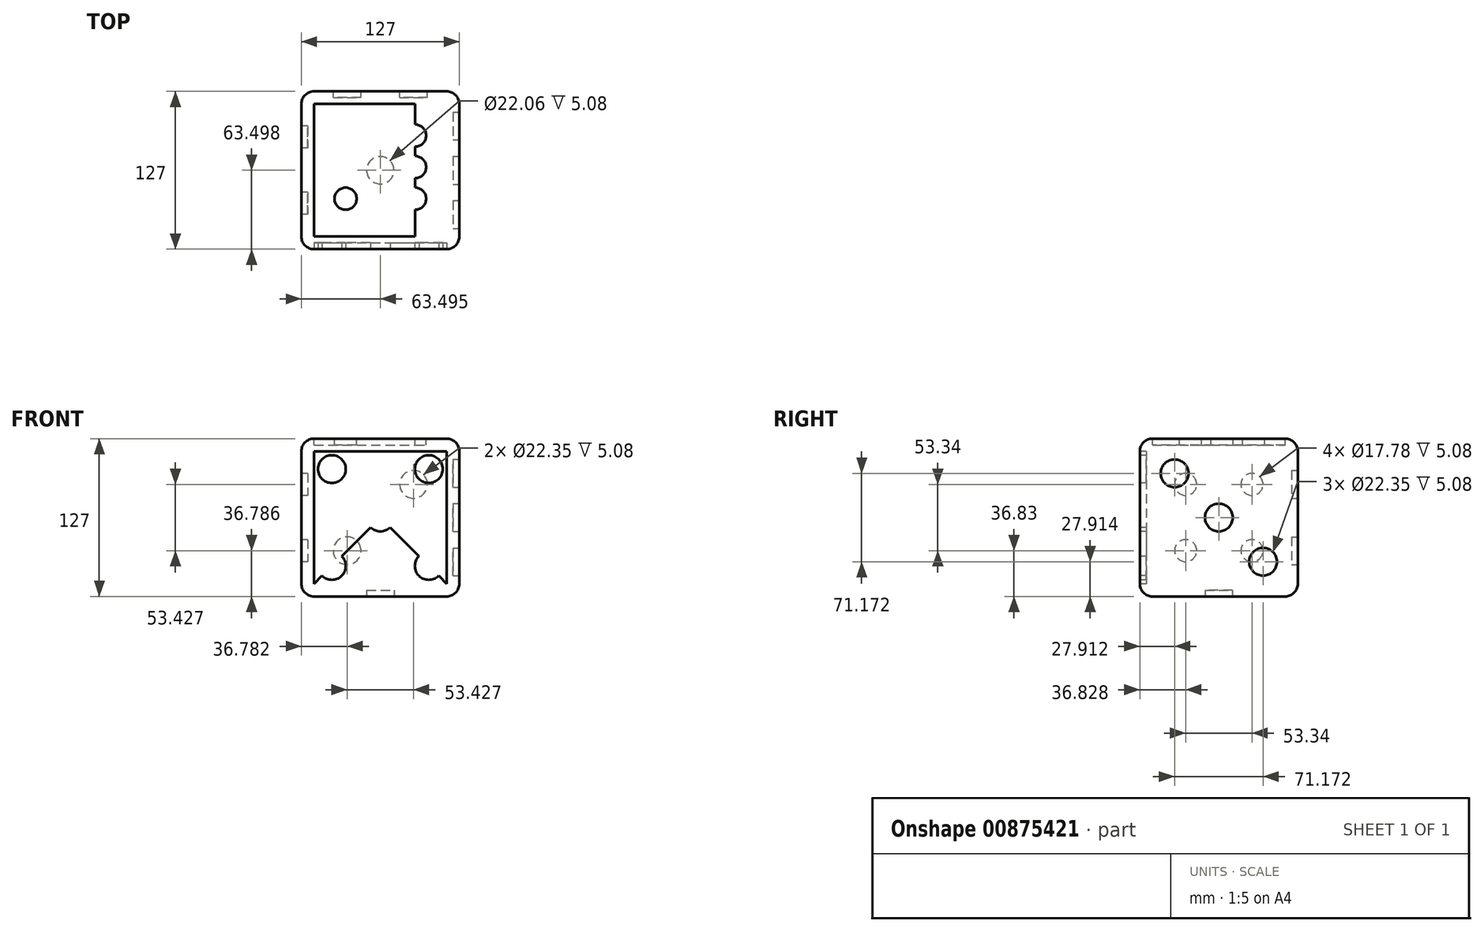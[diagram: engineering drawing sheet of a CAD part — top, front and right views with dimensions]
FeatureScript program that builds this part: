
annotation { "Feature Type Name" : "Feature", "Feature Type Description" : "" }
export const myFeature = defineFeature(function(context is Context, id is Id, definition is map)
    precondition{}
    {
        {
            var Q0;
            Q0=qCreatedBy(makeId("Top.planeOp"),FACE);
            var sketch = newSketch(context, id + "F0", { "sketchPlane" : qUnion([Q0])});
            skLineSegment(sketch, "E0.bottom", {"start": v(-135.56, 105.72) * mm, "end": v(-8.56, 105.72) * mm});
            skLineSegment(sketch, "E0.top", {"start": v(-135.56, -21.28) * mm, "end": v(-8.56, -21.28) * mm});
            skLineSegment(sketch, "E0.left", {"start": v(-135.56, 105.72) * mm, "end": v(-135.56, -21.28) * mm});
            skLineSegment(sketch, "E0.right", {"start": v(-8.56, 105.72) * mm, "end": v(-8.56, -21.28) * mm});
            skSolve(sketch);
        }
        {
            var Q0;
            Q0=makeQuery(id+"F0.imprint","IMPRINT",FACE,{"disambiguationData":[TD([[makeQuery(id+"F0.imprint","IMPRINT",EDGE,{"derivedFrom":sQuery(id+"F0.wireOp",EDGE,"E0.bottom")}),-1.0]])]});
            extrude(context, id + "F1", {"entities" : qUnion([Q0]), "depth" : 127 * mm, "offsetDistance" : 25.4 * mm});
        }
        {
            var Q0;
            Q0=makeQuery(id+"F1.opExtrude","SWEPT_FACE",FACE,{"disambiguationData":[OSD([sQuery(id+"F0.wireOp",EDGE,"E0.top")])]});
            var Q1;
            Q1=makeQuery(id+"F1.opExtrude","CAP_EDGE",EDGE,{"disambiguationData":[OSD([sQuery(id+"F0.wireOp",EDGE,"E0.bottom")])],"isStart":false});
            var Q2;
            Q2=makeQuery(id+"F1.opExtrude","CAP_FACE",FACE,{"disambiguationData":[OSD([sQuery(id+"F0.wireOp",EDGE,"E0.bottom"),sQuery(id+"F0.wireOp",EDGE,"E0.top"),sQuery(id+"F0.wireOp",EDGE,"E0.left"),sQuery(id+"F0.wireOp",EDGE,"E0.right")])],"isStart":false});
            var Q3;
            Q3=makeQuery(id+"F1.opExtrude","SWEPT_FACE",FACE,{"disambiguationData":[OSD([sQuery(id+"F0.wireOp",EDGE,"E0.left")])]});
            var Q4;
            Q4=makeQuery(id+"F1.opExtrude","SWEPT_FACE",FACE,{"disambiguationData":[OSD([sQuery(id+"F0.wireOp",EDGE,"E0.bottom")])]});
            var Q5;
            Q5=makeQuery(id+"F1.opExtrude","SWEPT_FACE",FACE,{"disambiguationData":[OSD([sQuery(id+"F0.wireOp",EDGE,"E0.right")])]});
            fillet(context, id + "F2", {"entities" : qUnion([Q0, Q1, Q2, Q3, Q4, Q5]), "radius" : 10.16 * mm, "tangentPropagation" : true, "allowEdgeOverflow" : false});
        }
        {
            var Q0;
            Q0=makeQuery(id+"F1.opExtrude","CAP_FACE",FACE,{"disambiguationData":[OSD([sQuery(id+"F0.wireOp",EDGE,"E0.bottom"),sQuery(id+"F0.wireOp",EDGE,"E0.top"),sQuery(id+"F0.wireOp",EDGE,"E0.left"),sQuery(id+"F0.wireOp",EDGE,"E0.right")])],"isStart":true});
            var sketch = newSketch(context, id + "F3", { "sketchPlane" : qUnion([Q0])});
            skPoint(sketch, "E1.0", {"position": v(-72.06, 11.12) * mm});
            skLineSegment(sketch, "E2.0", {"start": v(-125.4, 11.12) * mm, "end": v(-125.4, -95.56) * mm});
            skLineSegment(sketch, "E3.0", {"start": v(-18.72, -95.56) * mm, "end": v(-18.72, 11.12) * mm});
            skLineSegment(sketch, "E4.0", {"start": v(-125.4, -95.56) * mm, "end": v(-18.72, -95.56) * mm});
            skLineSegment(sketch, "E5", {"start": v(-72.06, 11.12) * mm, "end": v(-72.06, -95.56) * mm, "construction": true});
            skLineSegment(sketch, "E6", {"start": v(-125.4, -42.22) * mm, "end": v(-18.72, -42.22) * mm, "construction": true});
            skCircle(sketch, "E7", {"center": v(-72.06, -42.22) * mm, "radius": 11.03 * mm});
            skSolve(sketch);
        }
        {
            var Q0;
            Q0=makeQuery(id+"F3.imprint","IMPRINT",FACE,{"disambiguationData":[TD([[makeQuery(id+"F3.imprint","IMPRINT",EDGE,{"derivedFrom":sQuery(id+"F3.wireOp",EDGE,"E7")}),1.0]])]});
            extrude(context, id + "F4", {"entities" : qUnion([Q0]), "operationType" : NewBodyOperationType.REMOVE, "oppositeDirection" : true, "depth" : 5.08 * mm, "offsetDistance" : 25.4 * mm});
        }
        {
            var Q0;
            Q0=makeQuery(id+"F1.opExtrude","CAP_FACE",FACE,{"disambiguationData":[OSD([sQuery(id+"F0.wireOp",EDGE,"E0.bottom"),sQuery(id+"F0.wireOp",EDGE,"E0.top"),sQuery(id+"F0.wireOp",EDGE,"E0.left"),sQuery(id+"F0.wireOp",EDGE,"E0.right")])],"isStart":false});
            var sketch = newSketch(context, id + "F5", { "sketchPlane" : qUnion([Q0])});
            skLineSegment(sketch, "E8.0", {"start": v(-125.4, -11.12) * mm, "end": v(-18.72, -11.12) * mm});
            skLineSegment(sketch, "E9.0", {"start": v(-18.72, -11.12) * mm, "end": v(-18.72, 95.56) * mm});
            skLineSegment(sketch, "E10.0", {"start": v(-18.72, 95.56) * mm, "end": v(-125.4, 95.56) * mm});
            skLineSegment(sketch, "E11.0", {"start": v(-125.4, 95.56) * mm, "end": v(-125.4, -11.12) * mm});
            skLineSegment(sketch, "E12", {"start": v(-100, 95.56) * mm, "end": v(-100, -11.12) * mm});
            skLineSegment(sketch, "E13", {"start": v(-44.12, -11.12) * mm, "end": v(-44.12, 95.56) * mm});
            skCircle(sketch, "E14", {"center": v(-100, 70.16) * mm, "radius": 8.9 * mm});
            skCircle(sketch, "E15", {"center": v(-100, 19.36) * mm, "radius": 8.9 * mm});
            skCircle(sketch, "E16", {"center": v(-100, 44.76) * mm, "radius": 8.9 * mm});
            skCircle(sketch, "E17", {"center": v(-44.12, 70.16) * mm, "radius": 8.9 * mm});
            skCircle(sketch, "E18", {"center": v(-44.12, 44.76) * mm, "radius": 8.9 * mm});
            skCircle(sketch, "E19", {"center": v(-44.12, 19.36) * mm, "radius": 8.9 * mm});
            skSolve(sketch);
        }
        {
            var Q0;
            {var subQ0=sQuery(id+"F5.wireOp",EDGE,"E14");var subQ1=sQuery(id+"F5.wireOp",EDGE,"E12");var subQ2=makeQuery(id+"F5.imprint","INTERSECT",VERTEX,{"disambiguationData":[OD(0.0)],"derivedFrom":[subQ1,subQ0]});Q0=makeQuery(id+"F5.imprint","IMPRINT",FACE,{"disambiguationData":[TD([[makeQuery(id+"F5.imprint","IMPRINT",EDGE,{"disambiguationData":[TD([[subQ2,-1.0]])],"derivedFrom":subQ1}),-1.0]])]});}
            var Q1;
            {var subQ0=sQuery(id+"F5.wireOp",EDGE,"E14");var subQ1=sQuery(id+"F5.wireOp",EDGE,"E12");var subQ2=makeQuery(id+"F5.imprint","INTERSECT",VERTEX,{"disambiguationData":[OD(0.0)],"derivedFrom":[subQ1,subQ0]});Q1=makeQuery(id+"F5.imprint","IMPRINT",FACE,{"disambiguationData":[TD([[makeQuery(id+"F5.imprint","IMPRINT",EDGE,{"disambiguationData":[TD([[subQ2,-1.0]])],"derivedFrom":subQ1}),1.0]])]});}
            var Q2;
            {var subQ0=sQuery(id+"F5.wireOp",EDGE,"E16");var subQ1=sQuery(id+"F5.wireOp",EDGE,"E12");var subQ2=makeQuery(id+"F5.imprint","INTERSECT",VERTEX,{"disambiguationData":[OD(0.0)],"derivedFrom":[subQ1,subQ0]});Q2=makeQuery(id+"F5.imprint","IMPRINT",FACE,{"disambiguationData":[TD([[makeQuery(id+"F5.imprint","IMPRINT",EDGE,{"disambiguationData":[TD([[subQ2,-1.0]])],"derivedFrom":subQ1}),-1.0]])]});}
            var Q3;
            {var subQ0=sQuery(id+"F5.wireOp",EDGE,"E16");var subQ1=sQuery(id+"F5.wireOp",EDGE,"E12");var subQ2=makeQuery(id+"F5.imprint","INTERSECT",VERTEX,{"disambiguationData":[OD(0.0)],"derivedFrom":[subQ1,subQ0]});Q3=makeQuery(id+"F5.imprint","IMPRINT",FACE,{"disambiguationData":[TD([[makeQuery(id+"F5.imprint","IMPRINT",EDGE,{"disambiguationData":[TD([[subQ2,-1.0]])],"derivedFrom":subQ1}),1.0]])]});}
            var Q4;
            {var subQ0=sQuery(id+"F5.wireOp",EDGE,"E17");var subQ1=sQuery(id+"F5.wireOp",EDGE,"E13");var subQ2=makeQuery(id+"F5.imprint","INTERSECT",VERTEX,{"disambiguationData":[OD(0.0)],"derivedFrom":[subQ1,subQ0]});Q4=makeQuery(id+"F5.imprint","IMPRINT",FACE,{"disambiguationData":[TD([[makeQuery(id+"F5.imprint","IMPRINT",EDGE,{"disambiguationData":[TD([[subQ2,-1.0]])],"derivedFrom":subQ1}),1.0]])]});}
            var Q5;
            {var subQ0=sQuery(id+"F5.wireOp",EDGE,"E17");var subQ1=sQuery(id+"F5.wireOp",EDGE,"E13");var subQ2=makeQuery(id+"F5.imprint","INTERSECT",VERTEX,{"disambiguationData":[OD(0.0)],"derivedFrom":[subQ1,subQ0]});Q5=makeQuery(id+"F5.imprint","IMPRINT",FACE,{"disambiguationData":[TD([[makeQuery(id+"F5.imprint","IMPRINT",EDGE,{"disambiguationData":[TD([[subQ2,-1.0]])],"derivedFrom":subQ1}),-1.0]])]});}
            var Q6;
            {var subQ0=sQuery(id+"F5.wireOp",EDGE,"E18");var subQ1=sQuery(id+"F5.wireOp",EDGE,"E13");var subQ2=makeQuery(id+"F5.imprint","INTERSECT",VERTEX,{"disambiguationData":[OD(0.0)],"derivedFrom":[subQ1,subQ0]});Q6=makeQuery(id+"F5.imprint","IMPRINT",FACE,{"disambiguationData":[TD([[makeQuery(id+"F5.imprint","IMPRINT",EDGE,{"disambiguationData":[TD([[subQ2,-1.0]])],"derivedFrom":subQ1}),1.0]])]});}
            var Q7;
            {var subQ0=sQuery(id+"F5.wireOp",EDGE,"E18");var subQ1=sQuery(id+"F5.wireOp",EDGE,"E13");var subQ2=makeQuery(id+"F5.imprint","INTERSECT",VERTEX,{"disambiguationData":[OD(0.0)],"derivedFrom":[subQ1,subQ0]});Q7=makeQuery(id+"F5.imprint","IMPRINT",FACE,{"disambiguationData":[TD([[makeQuery(id+"F5.imprint","IMPRINT",EDGE,{"disambiguationData":[TD([[subQ2,-1.0]])],"derivedFrom":subQ1}),-1.0]])]});}
            var Q8;
            {var subQ0=sQuery(id+"F5.wireOp",EDGE,"E15");var subQ1=sQuery(id+"F5.wireOp",EDGE,"E12");var subQ2=makeQuery(id+"F5.imprint","INTERSECT",VERTEX,{"disambiguationData":[OD(0.0)],"derivedFrom":[subQ1,subQ0]});Q8=makeQuery(id+"F5.imprint","IMPRINT",FACE,{"disambiguationData":[TD([[makeQuery(id+"F5.imprint","IMPRINT",EDGE,{"disambiguationData":[TD([[subQ2,-1.0]])],"derivedFrom":subQ1}),-1.0]])]});}
            var Q9;
            {var subQ0=sQuery(id+"F5.wireOp",EDGE,"E15");var subQ1=sQuery(id+"F5.wireOp",EDGE,"E12");var subQ2=makeQuery(id+"F5.imprint","INTERSECT",VERTEX,{"disambiguationData":[OD(0.0)],"derivedFrom":[subQ1,subQ0]});Q9=makeQuery(id+"F5.imprint","IMPRINT",FACE,{"disambiguationData":[TD([[makeQuery(id+"F5.imprint","IMPRINT",EDGE,{"disambiguationData":[TD([[subQ2,-1.0]])],"derivedFrom":subQ1}),1.0]])]});}
            var Q10;
            {var subQ0=sQuery(id+"F5.wireOp",EDGE,"E19");var subQ1=sQuery(id+"F5.wireOp",EDGE,"E13");var subQ2=makeQuery(id+"F5.imprint","INTERSECT",VERTEX,{"disambiguationData":[OD(0.0)],"derivedFrom":[subQ1,subQ0]});Q10=makeQuery(id+"F5.imprint","IMPRINT",FACE,{"disambiguationData":[TD([[makeQuery(id+"F5.imprint","IMPRINT",EDGE,{"disambiguationData":[TD([[subQ2,-1.0]])],"derivedFrom":subQ1}),1.0]])]});}
            var Q11;
            {var subQ0=sQuery(id+"F5.wireOp",EDGE,"E19");var subQ1=sQuery(id+"F5.wireOp",EDGE,"E13");var subQ2=makeQuery(id+"F5.imprint","INTERSECT",VERTEX,{"disambiguationData":[OD(0.0)],"derivedFrom":[subQ1,subQ0]});Q11=makeQuery(id+"F5.imprint","IMPRINT",FACE,{"disambiguationData":[TD([[makeQuery(id+"F5.imprint","IMPRINT",EDGE,{"disambiguationData":[TD([[subQ2,-1.0]])],"derivedFrom":subQ1}),-1.0]])]});}
            extrude(context, id + "F6", {"entities" : qUnion([Q0, Q1, Q2, Q3, Q4, Q5, Q6, Q7, Q8, Q9, Q10, Q11]), "operationType" : NewBodyOperationType.REMOVE, "oppositeDirection" : true, "depth" : 5.08 * mm, "offsetDistance" : 25.4 * mm});
        }
        {
            var Q0;
            Q0=makeQuery(id+"F1.opExtrude","SWEPT_FACE",FACE,{"disambiguationData":[OSD([sQuery(id+"F0.wireOp",EDGE,"E0.left")])]});
            var sketch = newSketch(context, id + "F7", { "sketchPlane" : qUnion([Q0])});
            skLineSegment(sketch, "E20.0", {"start": v(11.12, 116.84) * mm, "end": v(-95.56, 116.84) * mm});
            skLineSegment(sketch, "E21.0", {"start": v(-95.56, 116.84) * mm, "end": v(-95.56, 10.16) * mm});
            skLineSegment(sketch, "E22.0", {"start": v(11.12, 10.16) * mm, "end": v(11.12, 116.84) * mm});
            skLineSegment(sketch, "E23.0", {"start": v(-95.56, 10.16) * mm, "end": v(11.12, 10.16) * mm});
            skCircle(sketch, "E24", {"center": v(-68.89, 90.17) * mm, "radius": 8.9 * mm});
            skCircle(sketch, "E25", {"center": v(-15.55, 90.17) * mm, "radius": 8.9 * mm});
            skCircle(sketch, "E26", {"center": v(-68.89, 36.83) * mm, "radius": 8.9 * mm});
            skCircle(sketch, "E27", {"center": v(-15.55, 36.83) * mm, "radius": 8.9 * mm});
            skSolve(sketch);
        }
        {
            var Q0;
            Q0=makeQuery(id+"F7.imprint","IMPRINT",FACE,{"disambiguationData":[TD([[makeQuery(id+"F7.imprint","IMPRINT",EDGE,{"derivedFrom":sQuery(id+"F7.wireOp",EDGE,"E24")}),1.0]])]});
            var Q1;
            Q1=makeQuery(id+"F7.imprint","IMPRINT",FACE,{"disambiguationData":[TD([[makeQuery(id+"F7.imprint","IMPRINT",EDGE,{"derivedFrom":sQuery(id+"F7.wireOp",EDGE,"E26")}),1.0]])]});
            var Q2;
            Q2=makeQuery(id+"F7.imprint","IMPRINT",FACE,{"disambiguationData":[TD([[makeQuery(id+"F7.imprint","IMPRINT",EDGE,{"derivedFrom":sQuery(id+"F7.wireOp",EDGE,"E27")}),1.0]])]});
            var Q3;
            Q3=makeQuery(id+"F7.imprint","IMPRINT",FACE,{"disambiguationData":[TD([[makeQuery(id+"F7.imprint","IMPRINT",EDGE,{"derivedFrom":sQuery(id+"F7.wireOp",EDGE,"E25")}),1.0]])]});
            extrude(context, id + "F8", {"entities" : qUnion([Q0, Q1, Q2, Q3]), "operationType" : NewBodyOperationType.REMOVE, "oppositeDirection" : true, "depth" : 5.08 * mm, "offsetDistance" : 25.4 * mm});
        }
        {
            var Q0;
            Q0=makeQuery(id+"F1.opExtrude","SWEPT_FACE",FACE,{"disambiguationData":[OSD([sQuery(id+"F0.wireOp",EDGE,"E0.right")])]});
            var sketch = newSketch(context, id + "F9", { "sketchPlane" : qUnion([Q0])});
            skCircle(sketch, "E28", {"center": v(77.8, 27.91) * mm, "radius": 11.18 * mm});
            skCircle(sketch, "E29", {"center": v(6.63, 99.09) * mm, "radius": 11.18 * mm});
            skCircle(sketch, "E30", {"center": v(42.22, 63.5) * mm, "radius": 11.18 * mm});
            skSolve(sketch);
        }
        {
            var Q0;
            Q0=makeQuery(id+"F9.imprint","IMPRINT",FACE,{"disambiguationData":[TD([[makeQuery(id+"F9.imprint","IMPRINT",EDGE,{"derivedFrom":sQuery(id+"F9.wireOp",EDGE,"E29")}),1.0]])]});
            var Q1;
            Q1=makeQuery(id+"F9.imprint","IMPRINT",FACE,{"disambiguationData":[TD([[makeQuery(id+"F9.imprint","IMPRINT",EDGE,{"derivedFrom":sQuery(id+"F9.wireOp",EDGE,"E28")}),1.0]])]});
            var Q2;
            Q2=makeQuery(id+"F9.imprint","IMPRINT",FACE,{"disambiguationData":[TD([[makeQuery(id+"F9.imprint","IMPRINT",EDGE,{"derivedFrom":sQuery(id+"F9.wireOp",EDGE,"E30")}),1.0]])]});
            extrude(context, id + "F10", {"entities" : qUnion([Q0, Q1, Q2]), "operationType" : NewBodyOperationType.REMOVE, "oppositeDirection" : true, "depth" : 5.08 * mm, "offsetDistance" : 25.4 * mm});
        }
        {
            var Q0;
            Q0=makeQuery(id+"F1.opExtrude","SWEPT_FACE",FACE,{"disambiguationData":[OSD([sQuery(id+"F0.wireOp",EDGE,"E0.top")])]});
            var sketch = newSketch(context, id + "F11", { "sketchPlane" : qUnion([Q0])});
            skLineSegment(sketch, "E31", {"start": v(-125.4, 116.84) * mm, "end": v(-18.72, 10.16) * mm});
            skLineSegment(sketch, "E32", {"start": v(-18.72, 116.84) * mm, "end": v(-125.4, 10.16) * mm});
            skCircle(sketch, "E33", {"center": v(-72.06, 63.5) * mm, "radius": 11.18 * mm});
            skCircle(sketch, "E34", {"center": v(-111.04, 102.47) * mm, "radius": 11.18 * mm});
            skCircle(sketch, "E35", {"center": v(-111.04, 24.53) * mm, "radius": 11.18 * mm});
            skCircle(sketch, "E36", {"center": v(-33.1, 24.53) * mm, "radius": 11.18 * mm});
            skCircle(sketch, "E37", {"center": v(-33.1, 102.47) * mm, "radius": 11.18 * mm});
            skSolve(sketch);
        }
        {
            var Q0;
            {var subQ0=sQuery(id+"F11.wireOp",EDGE,"E34");var subQ1=sQuery(id+"F11.wireOp",EDGE,"E31");var subQ2=makeQuery(id+"F11.imprint","INTERSECT",VERTEX,{"disambiguationData":[OD(0.0)],"derivedFrom":[subQ1,subQ0]});Q0=makeQuery(id+"F11.imprint","IMPRINT",FACE,{"disambiguationData":[TD([[makeQuery(id+"F11.imprint","IMPRINT",EDGE,{"disambiguationData":[TD([[subQ2,-1.0]])],"derivedFrom":subQ1}),1.0]])]});}
            var Q1;
            {var subQ0=sQuery(id+"F11.wireOp",EDGE,"E36");var subQ1=sQuery(id+"F11.wireOp",EDGE,"E31");var subQ2=makeQuery(id+"F11.imprint","INTERSECT",VERTEX,{"disambiguationData":[OD(0.0)],"derivedFrom":[subQ1,subQ0]});Q1=makeQuery(id+"F11.imprint","IMPRINT",FACE,{"disambiguationData":[TD([[makeQuery(id+"F11.imprint","IMPRINT",EDGE,{"disambiguationData":[TD([[subQ2,-1.0]])],"derivedFrom":subQ1}),-1.0]])]});}
            var Q2;
            {var subQ0=sQuery(id+"F11.wireOp",EDGE,"E36");var subQ1=sQuery(id+"F11.wireOp",EDGE,"E31");var subQ2=makeQuery(id+"F11.imprint","INTERSECT",VERTEX,{"disambiguationData":[OD(0.0)],"derivedFrom":[subQ1,subQ0]});Q2=makeQuery(id+"F11.imprint","IMPRINT",FACE,{"disambiguationData":[TD([[makeQuery(id+"F11.imprint","IMPRINT",EDGE,{"disambiguationData":[TD([[subQ2,-1.0]])],"derivedFrom":subQ1}),1.0]])]});}
            var Q3;
            {var subQ0=sQuery(id+"F11.wireOp",EDGE,"E35");var subQ1=sQuery(id+"F11.wireOp",EDGE,"E32");var subQ2=makeQuery(id+"F11.imprint","INTERSECT",VERTEX,{"disambiguationData":[OD(0.0)],"derivedFrom":[subQ1,subQ0]});Q3=makeQuery(id+"F11.imprint","IMPRINT",FACE,{"disambiguationData":[TD([[makeQuery(id+"F11.imprint","IMPRINT",EDGE,{"disambiguationData":[TD([[subQ2,-1.0]])],"derivedFrom":subQ1}),-1.0]])]});}
            var Q4;
            {var subQ0=sQuery(id+"F11.wireOp",EDGE,"E35");var subQ1=sQuery(id+"F11.wireOp",EDGE,"E32");var subQ2=makeQuery(id+"F11.imprint","INTERSECT",VERTEX,{"disambiguationData":[OD(0.0)],"derivedFrom":[subQ1,subQ0]});Q4=makeQuery(id+"F11.imprint","IMPRINT",FACE,{"disambiguationData":[TD([[makeQuery(id+"F11.imprint","IMPRINT",EDGE,{"disambiguationData":[TD([[subQ2,-1.0]])],"derivedFrom":subQ1}),1.0]])]});}
            var Q5;
            {var subQ0=sQuery(id+"F11.wireOp",EDGE,"E33");var subQ1=sQuery(id+"F11.wireOp",EDGE,"E31");var subQ2=makeQuery(id+"F11.imprint","INTERSECT",VERTEX,{"disambiguationData":[OD(0.0)],"derivedFrom":[subQ1,subQ0]});Q5=makeQuery(id+"F11.imprint","IMPRINT",FACE,{"disambiguationData":[TD([[makeQuery(id+"F11.imprint","IMPRINT",EDGE,{"disambiguationData":[TD([[subQ2,-1.0]])],"derivedFrom":subQ1}),1.0]])]});}
            var Q6;
            {var subQ0=sQuery(id+"F11.wireOp",EDGE,"E33");var subQ1=sQuery(id+"F11.wireOp",EDGE,"E31");var subQ2=makeQuery(id+"F11.imprint","INTERSECT",VERTEX,{"disambiguationData":[OD(0.0)],"derivedFrom":[subQ1,subQ0]});Q6=makeQuery(id+"F11.imprint","IMPRINT",FACE,{"disambiguationData":[TD([[makeQuery(id+"F11.imprint","IMPRINT",EDGE,{"disambiguationData":[TD([[subQ2,-1.0]])],"derivedFrom":subQ1}),-1.0]])]});}
            var Q7;
            {var subQ0=sQuery(id+"F11.wireOp",EDGE,"E32");var subQ1=sQuery(id+"F11.wireOp",EDGE,"E31");var subQ2=makeQuery(id+"F11.imprint","INTERSECT",VERTEX,{"derivedFrom":[subQ1,subQ0]});Q7=makeQuery(id+"F11.imprint","IMPRINT",FACE,{"disambiguationData":[TD([[makeQuery(id+"F11.imprint","IMPRINT",EDGE,{"disambiguationData":[TD([[subQ2,-1.0]])],"derivedFrom":subQ1}),1.0]])]});}
            var Q8;
            {var subQ0=sQuery(id+"F11.wireOp",EDGE,"E32");var subQ1=sQuery(id+"F11.wireOp",EDGE,"E31");var subQ2=makeQuery(id+"F11.imprint","INTERSECT",VERTEX,{"derivedFrom":[subQ1,subQ0]});Q8=makeQuery(id+"F11.imprint","IMPRINT",FACE,{"disambiguationData":[TD([[makeQuery(id+"F11.imprint","IMPRINT",EDGE,{"disambiguationData":[TD([[subQ2,-1.0]])],"derivedFrom":subQ1}),-1.0]])]});}
            var Q9;
            {var subQ0=sQuery(id+"F11.wireOp",EDGE,"E34");var subQ1=sQuery(id+"F11.wireOp",EDGE,"E31");var subQ2=makeQuery(id+"F11.imprint","INTERSECT",VERTEX,{"disambiguationData":[OD(0.0)],"derivedFrom":[subQ1,subQ0]});Q9=makeQuery(id+"F11.imprint","IMPRINT",FACE,{"disambiguationData":[TD([[makeQuery(id+"F11.imprint","IMPRINT",EDGE,{"disambiguationData":[TD([[subQ2,-1.0]])],"derivedFrom":subQ1}),-1.0]])]});}
            var Q10;
            {var subQ0=sQuery(id+"F11.wireOp",EDGE,"E37");var subQ1=sQuery(id+"F11.wireOp",EDGE,"E32");var subQ2=makeQuery(id+"F11.imprint","INTERSECT",VERTEX,{"disambiguationData":[OD(0.0)],"derivedFrom":[subQ1,subQ0]});Q10=makeQuery(id+"F11.imprint","IMPRINT",FACE,{"disambiguationData":[TD([[makeQuery(id+"F11.imprint","IMPRINT",EDGE,{"disambiguationData":[TD([[subQ2,-1.0]])],"derivedFrom":subQ1}),-1.0]])]});}
            var Q11;
            {var subQ0=sQuery(id+"F11.wireOp",EDGE,"E37");var subQ1=sQuery(id+"F11.wireOp",EDGE,"E32");var subQ2=makeQuery(id+"F11.imprint","INTERSECT",VERTEX,{"disambiguationData":[OD(0.0)],"derivedFrom":[subQ1,subQ0]});Q11=makeQuery(id+"F11.imprint","IMPRINT",FACE,{"disambiguationData":[TD([[makeQuery(id+"F11.imprint","IMPRINT",EDGE,{"disambiguationData":[TD([[subQ2,-1.0]])],"derivedFrom":subQ1}),1.0]])]});}
            extrude(context, id + "F12", {"entities" : qUnion([Q0, Q1, Q2, Q3, Q4, Q5, Q6, Q7, Q8, Q9, Q10, Q11]), "operationType" : NewBodyOperationType.REMOVE, "oppositeDirection" : true, "depth" : 5.08 * mm, "offsetDistance" : 25.4 * mm});
        }
        {
            var Q0;
            Q0=makeQuery(id+"F1.opExtrude","SWEPT_FACE",FACE,{"disambiguationData":[OSD([sQuery(id+"F0.wireOp",EDGE,"E0.bottom")])]});
            var sketch = newSketch(context, id + "F13", { "sketchPlane" : qUnion([Q0])});
            skLineSegment(sketch, "E38", {"start": v(125.4, 10.16) * mm, "end": v(18.72, 116.84) * mm});
            skCircle(sketch, "E39", {"center": v(45.35, 90.21) * mm, "radius": 11.18 * mm});
            skCircle(sketch, "E40", {"center": v(98.78, 36.79) * mm, "radius": 11.18 * mm});
            skSolve(sketch);
        }
        {
            var Q0;
            Q0 = qSketchRegion(id + "F13", true);
            extrude(context, id + "F14", {"entities" : qUnion([Q0]), "operationType" : NewBodyOperationType.REMOVE, "oppositeDirection" : true, "depth" : 5.08 * mm, "offsetDistance" : 25.4 * mm});
        }
    });
